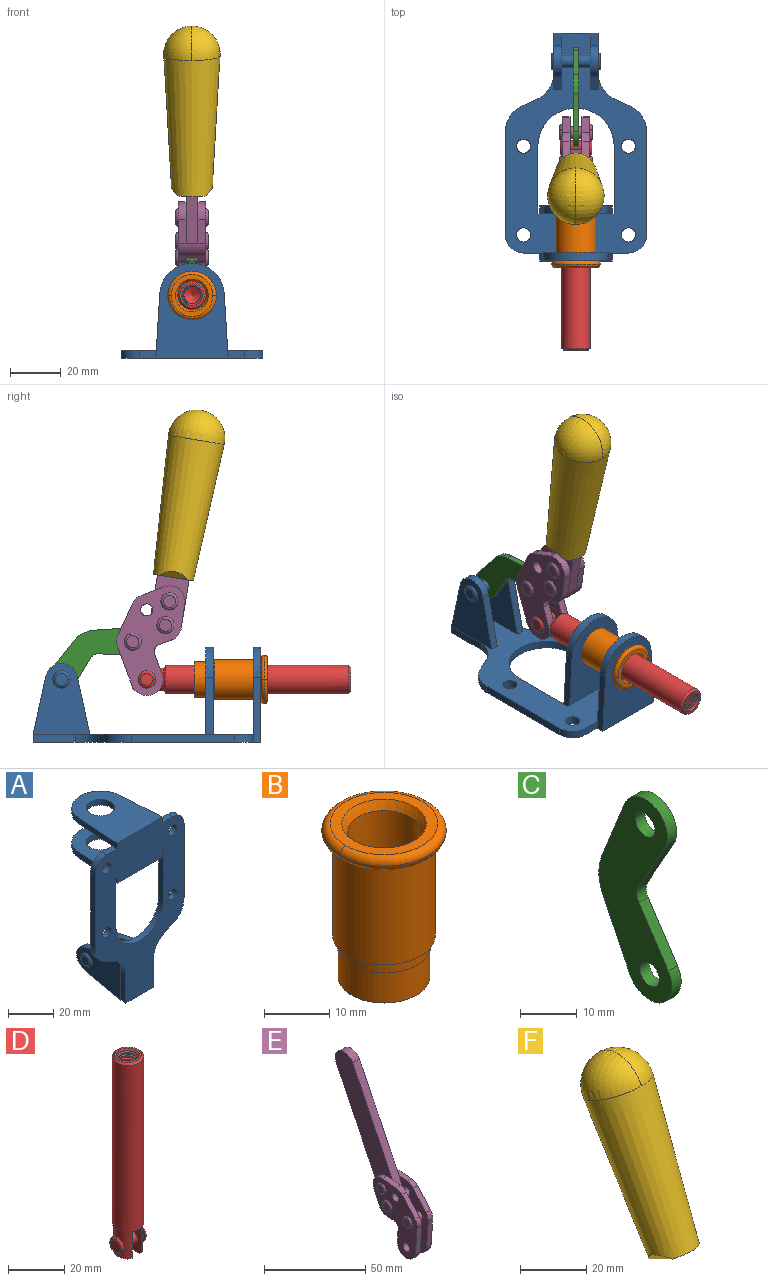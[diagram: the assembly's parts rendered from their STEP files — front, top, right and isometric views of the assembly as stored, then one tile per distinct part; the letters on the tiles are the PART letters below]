
ASSEMBLY  parts=6 mates=6
PART A: 55 faces, bbox 55.7x37.4x89.8 mm
  f0: torus R=2.41mm, axis (-1,0,0), area 15mm2, adj f11,f15,f25
  f1: torus R=2.41mm, axis (-1,0,0), area 15mm2, adj f10,f12,f22
  f2: cylinder r=2.78mm len=5.56mm, axis (0,-1,0), area 54.2mm2, adj f30,f54
  f3: cylinder r=14.99mm len=29.97mm, axis (0,-1,0), area 145.9mm2, adj f30,f49,f53,f54
  f4: cylinder r=2.78mm len=5.56mm, axis (0,-1,0), area 54.2mm2, adj f30,f54
  f5: cylinder r=2.78mm len=5.56mm, axis (0,-1,0), area 54.2mm2, adj f30,f54
  f6: cylinder r=2.78mm len=5.56mm, axis (0,-1,0), area 54.2mm2, adj f30,f54
  f7: cylinder r=6.35mm len=12.7mm, axis (0,0,1), area 123.6mm2, adj f27,f51
  f8: cylinder r=6.35mm len=12.7mm, axis (0,0,-1), area 124.7mm2, adj f21,f35
  f9: cylinder r=2.41mm len=11.18mm, axis (-1,0,0), area 169.4mm2, adj f16,f19
  f10: plane 4.83x4.83mm, normal (1,0,0), area 18.3mm2, adj f1,f12
  f11: plane 4.83x4.83mm, normal (-1,0,0), area 18.3mm2, adj f0,f15
  f12: torus R=2.41mm, axis (-1,0,0), area 15mm2, adj f1,f10,f22
  f13: cylinder r=6.35mm len=12.41mm, axis (1,0,0), area 53.4mm2, adj f18,f19,f22,f23
  f14: cylinder r=6.35mm len=12.41mm, axis (-1,0,0), area 53.4mm2, adj f16,f17,f24,f25
  f15: torus R=2.41mm, axis (-1,0,0), area 15mm2, adj f0,f11,f25
  f16: plane 27.86x22.35mm, normal (1,0,0), area 425.4mm2, adj f9,f14,f17,f24,f30
  f17: plane 22.86x4.97mm, normal (0,0.21,0.98), area 72.5mm2, adj f14,f16,f25,f30
  f18: plane 22.86x4.97mm, normal (0,0.21,0.98), area 72.5mm2, adj f13,f19,f22,f30
  f19: plane 27.86x22.35mm, normal (-1,0,0), area 425.4mm2, adj f9,f13,f18,f23,f30
  f20: cylinder r=12.7mm len=25.35mm, axis (0,0,-1), area 119.8mm2, adj f21,f34,f35,f36
  f21: plane 34.21x28.07mm, normal (0,0,-1), area 702.4mm2, adj f8,f20,f30,f34,f36
  f22: plane 27.96x22.45mm, normal (1,0,0), area 407.2mm2, adj f1,f12,f13,f18,f23,f30,f42,f43
  f23: plane 22.86x4.97mm, normal (0,0.21,-0.98), area 72.5mm2, adj f13,f19,f22,f44
  f24: plane 22.86x4.97mm, normal (0,0.21,-0.98), area 72.5mm2, adj f14,f16,f25,f44
  f25: plane 27.86x22.35mm, normal (-1,0,0), area 407.1mm2, adj f0,f14,f15,f17,f24,f30,f45,f46
  f26: plane 3.1x0.95mm, normal (0,0,-1), area 2.7mm2, adj f30,f49,f50,f54
  f27: plane 34.21x28.07mm, normal (0,0,1), area 702.4mm2, adj f7,f28,f30,f50,f52
  f28: cylinder r=12.7mm len=25.35mm, axis (0,0,1), area 118.8mm2, adj f27,f50,f51,f52
  f29: plane 3.1x0.95mm, normal (0,0,-1), area 2.7mm2, adj f30,f52,f53,f54
  f30: plane 86.54x55.63mm, normal (0,1,0), area 2362.9mm2, adj f2,f3,f4,f5,f6,f16,f17,f18
  f31: plane 40.56x3.1mm, normal (-1,0,0), area 125.7mm2, adj f30,f32,f48,f54
  f32: cylinder r=7.11mm len=7.11mm, axis (0,-1,0), area 34.6mm2, adj f30,f31,f33,f54
  f33: plane 6.67x3.1mm, normal (0,0,1), area 20.4mm2, adj f30,f32,f34,f54
  f34: plane 25.39x3.13mm, normal (-1,0.06,0), area 79.5mm2, adj f20,f21,f33,f35,f54
  f35: plane 37.31x28.45mm, normal (0,0,1), area 789.9mm2, adj f8,f20,f34,f36,f54
  f36: plane 25.39x3.13mm, normal (1,0.06,0), area 79.5mm2, adj f20,f21,f35,f37,f54
  f37: plane 6.67x3.1mm, normal (0,0,1), area 20.4mm2, adj f30,f36,f38,f54
  f38: cylinder r=7.11mm len=7.11mm, axis (0,-1,0), area 34.6mm2, adj f30,f37,f39,f54
  f39: plane 40.56x3.1mm, normal (1,0,0), area 125.7mm2, adj f30,f38,f40,f54
  f40: cylinder r=11.18mm len=10.16mm, axis (0,-1,0), area 39.5mm2, adj f30,f39,f41,f54
  f41: plane 6.09x3.1mm, normal (0.42,0,-0.91), area 20.8mm2, adj f30,f40,f42,f54
  f42: cylinder r=11.18mm len=9.41mm, axis (0,-1,0), area 37.2mm2, adj f22,f30,f41,f43,f54
  f43: plane 16.5x3.1mm, normal (1,0,0), area 51.1mm2, adj f22,f42,f44,f54
  f44: plane 17.37x3.1mm, normal (0,0,-1), area 53.8mm2, adj f23,f24,f30,f43,f45,f54
  f45: plane 16.5x3.1mm, normal (-1,0,0), area 51.1mm2, adj f25,f44,f46,f54
  f46: cylinder r=11.18mm len=9.41mm, axis (0,-1,0), area 37.2mm2, adj f25,f30,f45,f47,f54
  f47: plane 6.09x3.1mm, normal (-0.42,0,-0.91), area 20.8mm2, adj f30,f46,f48,f54
  f48: cylinder r=11.18mm len=10.16mm, axis (0,-1,0), area 39.5mm2, adj f30,f31,f47,f54
  f49: plane 26.54x3.1mm, normal (-1,0,0), area 82.3mm2, adj f3,f26,f30,f54
  f50: plane 25.39x3.1mm, normal (1,0.06,0), area 78.8mm2, adj f26,f27,f28,f51,f54
  f51: plane 37.31x28.45mm, normal (0,0,-1), area 789.9mm2, adj f7,f28,f50,f52,f54
  f52: plane 25.39x3.1mm, normal (-1,0.06,0), area 78.8mm2, adj f27,f28,f29,f51,f54
  f53: plane 26.54x3.1mm, normal (1,0,0), area 82.3mm2, adj f3,f29,f30,f54
  f54: plane 89.66x55.63mm, normal (0,-1,0), area 2678.5mm2, adj f2,f3,f4,f5,f6,f26,f29,f31
PART B: 15 faces, bbox 20.6x20.6x28.7 mm
  f0: torus R=8.26mm, axis (0,0,1), area 56.8mm2, adj f1,f10,f12
  f1: torus R=8.26mm, axis (0,0,1), area 56.8mm2, adj f0,f6,f13
  f2: cylinder r=5.59mm len=25.91mm, axis (0,0,1), area 909.6mm2, adj f3,f4
  f3: cone r=6.86mm half-angle=45deg, axis (0,0,-1), area 70.2mm2, adj f2,f14
  f4: cone r=6.47mm half-angle=30deg, axis (0,0,1), area 66.7mm2, adj f2,f13
  f5: cylinder r=7.04mm len=14.07mm, axis (0,0,1), area 252.6mm2, adj f11,f14
  f6: torus R=8.26mm, axis (0,0,1), area 56.8mm2, adj f1,f12,f13
  f7: cylinder r=7.16mm len=14.33mm, axis (0,0,1), area 91.5mm2, adj f9,f11
  f8: cylinder r=7.86mm len=18.42mm, axis (0,0,1), area 909.6mm2, adj f9,f10
  f9: plane 15.72x15.72mm, normal (0,0,-1), area 33mm2, adj f7,f8
  f10: plane 16.51x16.51mm, normal (0,0,-1), area 19.9mm2, adj f0,f8,f12
  f11: plane 14.33x14.33mm, normal (0,0,-1), area 5.7mm2, adj f5,f7
  f12: torus R=8.26mm, axis (0,0,1), area 56.8mm2, adj f0,f6,f10
  f13: plane 16.51x16.51mm, normal (0,0,1), area 82.7mm2, adj f1,f4,f6
  f14: plane 14.07x14.07mm, normal (0,0,-1), area 7.8mm2, adj f3,f5
PART C: 12 faces, bbox 2.3x18.2x42.8 mm
  f0: cylinder r=2.4mm len=4.8mm, axis (1,0,0), area 34.9mm2, adj f4,f11
  f1: cylinder r=10.41mm len=8.47mm, axis (1,0,0), area 20.2mm2, adj f4,f9,f10,f11
  f2: cylinder r=3.05mm len=3.16mm, axis (1,0,0), area 7.7mm2, adj f4,f6,f7,f11
  f3: cylinder r=2.4mm len=4.8mm, axis (1,0,0), area 34.9mm2, adj f4,f11
  f4: plane 42.81x18.23mm, normal (-1,0,0), area 414.1mm2, adj f0,f1,f2,f3,f5,f6,f7,f8
  f5: cylinder r=5.54mm len=10.67mm, axis (1,0,0), area 41.8mm2, adj f4,f6,f10,f11
  f6: plane 11.66x6.53mm, normal (0,-0.87,-0.49), area 30.9mm2, adj f2,f4,f5,f11
  f7: plane 11.17x7.33mm, normal (0,-0.84,0.55), area 30.9mm2, adj f2,f4,f8,f11
  f8: cylinder r=5.54mm len=10.51mm, axis (1,0,0), area 41.8mm2, adj f4,f7,f9,f11
  f9: plane 13.67x6.67mm, normal (0,0.9,-0.44), area 35.1mm2, adj f1,f4,f8,f11
  f10: plane 14.1x5.7mm, normal (0,0.93,0.37), area 35.1mm2, adj f1,f4,f5,f11
  f11: plane 42.81x18.23mm, normal (1,0,0), area 414.1mm2, adj f0,f1,f2,f3,f5,f6,f7,f8
PART D: 48 faces, bbox 12.6x11.1x86.1 mm
  f0: torus R=2.41mm, axis (-1,0,0), area 15mm2, adj f30,f32,f34
  f1: torus R=2.41mm, axis (-1,0,0), area 15mm2, adj f29,f31,f33
  f2: cylinder r=5.54mm len=72.39mm, axis (0,0,1), area 2518.5mm2, adj f3,f4,f42,f43
  f3: cone r=5.54mm half-angle=45deg, axis (0,0,1), area 7.6mm2, adj f2,f5,f41
  f4: cone r=5.54mm half-angle=45deg, axis (0,0,-1), area 34.9mm2, adj f2,f39
  f5: cylinder r=5.08mm len=11.48mm, axis (0,0,1), area 108.3mm2, adj f3,f7,f8,f41
  f6: cylinder r=2.41mm len=4.83mm, axis (-1,0,0), area 71.2mm2, adj f40,f41
  f7: cylinder r=2.41mm len=4.83mm, axis (-1,0,0), area 7.6mm2, adj f5,f34
  f8: cone r=5.08mm half-angle=45deg, axis (0,0,1), area 10.6mm2, adj f5,f37,f41
  f9: cone r=3.98mm half-angle=45deg, axis (0,0,1), area 17.6mm2, adj f27,f39,f45,f46,f47
  f10: cylinder r=2.41mm len=4.83mm, axis (-1,0,0), area 7.6mm2, adj f33,f38
  f11: cylinder r=3.2mm len=6.4mm, axis (0,0,1), area 78.4mm2, adj f12,f28,f44,f45,f47
  f12: cylinder r=3.2mm len=6.4mm, axis (0,0,1), area 10.5mm2, adj f11,f13,f45,f47
  f13: cylinder r=3.2mm len=6.4mm, axis (0,0,1), area 10.5mm2, adj f12,f14,f45,f47
  f14: cylinder r=3.2mm len=6.4mm, axis (0,0,1), area 10.5mm2, adj f13,f15,f45,f47
  f15: cylinder r=3.2mm len=6.4mm, axis (0,0,1), area 10.5mm2, adj f14,f16,f45,f47
  f16: cylinder r=3.2mm len=6.4mm, axis (0,0,1), area 10.5mm2, adj f15,f17,f45,f47
  f17: cylinder r=3.2mm len=6.4mm, axis (0,0,1), area 10.5mm2, adj f16,f18,f45,f47
  f18: cylinder r=3.2mm len=6.4mm, axis (0,0,1), area 10.5mm2, adj f17,f19,f45,f47
  f19: cylinder r=3.2mm len=6.4mm, axis (0,0,1), area 10.5mm2, adj f18,f20,f45,f47
  f20: cylinder r=3.2mm len=6.4mm, axis (0,0,1), area 10.5mm2, adj f19,f21,f45,f47
  f21: cylinder r=3.2mm len=6.4mm, axis (0,0,1), area 10.5mm2, adj f20,f22,f45,f47
  f22: cylinder r=3.2mm len=6.4mm, axis (0,0,1), area 10.5mm2, adj f21,f23,f45,f47
  f23: cylinder r=3.2mm len=6.4mm, axis (0,0,1), area 10.5mm2, adj f22,f24,f45,f47
  f24: cylinder r=3.2mm len=6.4mm, axis (0,0,1), area 10.5mm2, adj f23,f25,f45,f47
  f25: cylinder r=3.2mm len=6.4mm, axis (0,0,1), area 10.5mm2, adj f24,f26,f45,f47
  f26: cylinder r=3.2mm len=6.4mm, axis (0,0,1), area 10.5mm2, adj f25,f27,f45,f47
  f27: cylinder r=3.2mm len=6.4mm, axis (0,0,1), area 7.4mm2, adj f9,f26,f45,f47
  f28: cone r=3.2mm half-angle=60deg, axis (0,0,1), area 37.2mm2, adj f11
  f29: plane 4.83x4.83mm, normal (-1,0,0), area 18.3mm2, adj f1,f31
  f30: plane 4.83x4.83mm, normal (1,0,0), area 18.3mm2, adj f0,f32
  f31: torus R=2.41mm, axis (-1,0,0), area 15mm2, adj f1,f29,f33
  f32: torus R=2.41mm, axis (-1,0,0), area 15mm2, adj f0,f30,f34
  f33: plane 6.83x6.83mm, normal (1,0,0), area 18.3mm2, adj f1,f10,f31
  f34: plane 6.83x6.83mm, normal (-1,0,0), area 18.3mm2, adj f0,f7,f32
  f35: cone r=5.08mm half-angle=45deg, axis (0,0,1), area 10.6mm2, adj f36,f38,f40
  f36: plane 7.25x1.97mm, normal (0,0,-1), area 10mm2, adj f35,f40
  f37: plane 7.25x1.97mm, normal (0,0,-1), area 10mm2, adj f8,f41
  f38: cylinder r=5.08mm len=11.48mm, axis (0,0,1), area 108.3mm2, adj f10,f35,f40,f42
  f39: plane 9.55x9.55mm, normal (0,0,1), area 22mm2, adj f4,f9
  f40: plane 12.76x10.09mm, normal (1,0,0), area 95.7mm2, adj f6,f35,f36,f38,f42,f43
  f41: plane 12.76x10.09mm, normal (-1,0,0), area 95.7mm2, adj f3,f5,f6,f8,f37,f43
  f42: cone r=5.54mm half-angle=45deg, axis (0,0,1), area 7.6mm2, adj f2,f38,f40
  f43: plane 11.07x4.7mm, normal (0,0,-1), area 50.4mm2, adj f2,f40,f41
  f44: plane 0.89x0.62mm, normal (-1,0,0), area 0.3mm2, adj f11,f45,f46,f47
  f45: bspline ~24.8x7.63mm, area 266.6mm2, adj f9,f11,f12,f13,f14,f15,f16,f17
  f46: bspline ~24.87x7.63mm, area 73.6mm2, adj f9,f44,f45,f47
  f47: bspline ~24.98x7.63mm, area 272.5mm2, adj f9,f11,f12,f13,f14,f15,f16,f17
PART E: 59 faces, bbox 12.9x60.2x99.6 mm
  f0: torus R=2.39mm, axis (-1,0,0), area 14.9mm2, adj f20,f43,f51
  f1: torus R=2.39mm, axis (-1,0,0), area 14.9mm2, adj f19,f42,f51
  f2: torus R=2.39mm, axis (-1,0,0), area 14.9mm2, adj f18,f35,f51
  f3: torus R=2.39mm, axis (-1,0,0), area 14.9mm2, adj f14,f17,f23
  f4: torus R=2.39mm, axis (-1,0,0), area 14.9mm2, adj f13,f16,f23
  f5: torus R=2.39mm, axis (-1,0,0), area 14.9mm2, adj f12,f15,f23
  f6: cylinder r=2.39mm len=4.78mm, axis (1,0,0), area 46.5mm2, adj f48,f50,f51
  f7: cylinder r=2.39mm len=4.78mm, axis (1,0,0), area 46.5mm2, adj f50,f51
  f8: cylinder r=6.35mm len=12.68mm, axis (1,0,0), area 61.8mm2, adj f38,f39,f50,f51
  f9: cylinder r=2.39mm len=4.78mm, axis (-1,0,0), area 70.5mm2, adj f46,f50
  f10: cylinder r=2.39mm len=4.78mm, axis (-1,0,0), area 46.5mm2, adj f23,f45,f46
  f11: cylinder r=2.39mm len=4.78mm, axis (-1,0,0), area 46.5mm2, adj f23,f46
  f12: plane 4.78x4.78mm, normal (1,0,0), area 17.9mm2, adj f5,f15
  f13: plane 4.78x4.78mm, normal (1,0,0), area 17.9mm2, adj f4,f16
  f14: plane 4.78x4.78mm, normal (1,0,0), area 17.9mm2, adj f3,f17
  f15: torus R=2.39mm, axis (-1,0,0), area 14.9mm2, adj f5,f12,f23
  f16: torus R=2.39mm, axis (-1,0,0), area 14.9mm2, adj f4,f13,f23
  f17: torus R=2.39mm, axis (-1,0,0), area 14.9mm2, adj f3,f14,f23
  f18: plane 4.78x4.78mm, normal (-1,0,0), area 17.9mm2, adj f2,f35
  f19: plane 4.78x4.78mm, normal (-1,0,0), area 17.9mm2, adj f1,f42
  f20: plane 4.78x4.78mm, normal (-1,0,0), area 17.9mm2, adj f0,f43
  f21: plane 2.26x0.2mm, normal (1,0,0), area 0.2mm2, adj f31,f44
  f22: plane 2.26x0.2mm, normal (-1,0,0), area 0.2mm2, adj f41,f44
  f23: plane 39.37x30.77mm, normal (1,0,0), area 565.5mm2, adj f3,f4,f5,f10,f11,f15,f16,f17
  f24: cylinder r=6.1mm len=4.15mm, axis (-1,0,0), area 14.7mm2, adj f23,f25,f32,f46
  f25: plane 10.25x9.01mm, normal (0,-0.75,0.66), area 42.3mm2, adj f23,f24,f26,f46
  f26: cylinder r=6.35mm len=4.64mm, axis (-1,0,0), area 15.6mm2, adj f23,f25,f27,f46
  f27: plane 15.84x3.1mm, normal (0,-1,-0.07), area 49.2mm2, adj f23,f26,f28,f46
  f28: cylinder r=6.35mm len=12.68mm, axis (-1,0,0), area 61.8mm2, adj f23,f27,f29,f46
  f29: plane 8.11x3.1mm, normal (0,1,0.07), area 25.2mm2, adj f23,f28,f30,f46
  f30: cylinder r=3.05mm len=3.25mm, axis (-1,0,0), area 14.8mm2, adj f23,f29,f31,f46
  f31: plane 5.99x3.1mm, normal (0,0.07,-1), area 18.6mm2, adj f21,f23,f30,f44,f46
  f32: plane 9.5x3.1mm, normal (0,-0.07,1), area 29.5mm2, adj f23,f24,f33,f46,f47
  f33: cylinder r=6.1mm len=8.63mm, axis (-1,0,0), area 39.1mm2, adj f23,f32,f34,f47
  f34: plane 8.65x3.96mm, normal (0,0.91,-0.42), area 29.5mm2, adj f23,f33,f44,f47
  f35: torus R=2.39mm, axis (-1,0,0), area 14.9mm2, adj f2,f18,f51
  f36: plane 10.25x9.01mm, normal (0,-0.75,0.66), area 42.3mm2, adj f37,f49,f50,f51
  f37: cylinder r=6.35mm len=4.64mm, axis (1,0,0), area 15.6mm2, adj f36,f38,f50,f51
  f38: plane 15.84x3.1mm, normal (0,-1,-0.07), area 49.2mm2, adj f8,f37,f50,f51
  f39: plane 8.11x3.1mm, normal (0,1,0.07), area 25.2mm2, adj f8,f40,f50,f51
  f40: cylinder r=3.05mm len=3.25mm, axis (1,0,0), area 14.8mm2, adj f39,f41,f50,f51
  f41: plane 5.99x3.1mm, normal (0,0.07,-1), area 18.6mm2, adj f22,f40,f44,f50,f51
  f42: torus R=2.39mm, axis (-1,0,0), area 14.9mm2, adj f1,f19,f51
  f43: torus R=2.39mm, axis (-1,0,0), area 14.9mm2, adj f0,f20,f51
  f44: cylinder r=6.35mm len=12.12mm, axis (-1,0,0), area 128.9mm2, adj f21,f22,f23,f31,f34,f41,f46,f47
  f45: plane 2.65x1.35mm, normal (1,0,0), area 1mm2, adj f10,f55
  f46: plane 39.08x20.42mm, normal (-1,0,0), area 412.5mm2, adj f9,f10,f11,f24,f25,f26,f27,f28
  f47: plane 77.62x39.82mm, normal (1,0,0), area 850mm2, adj f32,f33,f34,f44,f53,f54,f55
  f48: plane 2.65x1.35mm, normal (-1,0,0), area 1mm2, adj f6,f55
  f49: cylinder r=6.1mm len=4.15mm, axis (1,0,0), area 14.7mm2, adj f36,f50,f51,f56
  f50: plane 39.08x20.42mm, normal (1,0,0), area 412.5mm2, adj f6,f7,f8,f9,f36,f37,f38,f39
  f51: plane 39.37x30.77mm, normal (-1,0,0), area 565.5mm2, adj f0,f1,f2,f6,f7,f8,f35,f36
  f52: plane 8.65x3.96mm, normal (0,0.91,-0.42), area 29.5mm2, adj f44,f51,f57,f58
  f53: plane 68.49x33.4mm, normal (0,0.9,-0.44), area 358.1mm2, adj f44,f47,f54,f58
  f54: cylinder r=6.35mm len=12.06mm, axis (1,0,0), area 93.7mm2, adj f47,f53,f55,f58
  f55: plane 68.49x33.4mm, normal (0,-0.9,0.44), area 358.1mm2, adj f44,f45,f46,f47,f48,f50,f54,f58
  f56: plane 9.5x3.1mm, normal (0,-0.07,1), area 29.5mm2, adj f49,f50,f51,f57,f58
  f57: cylinder r=6.1mm len=8.63mm, axis (1,0,0), area 39.1mm2, adj f51,f52,f56,f58
  f58: plane 77.62x39.82mm, normal (-1,0,0), area 850mm2, adj f44,f52,f53,f54,f55,f56,f57
PART F: 11 faces, bbox 22.3x42.6x64.5 mm
  f0: sphere r=11.13mm, area 411.4mm2, adj f1,f8
  f1: cone r=11.11mm half-angle=3.3deg, axis (0,0.44,0.9), area 3251.8mm2, adj f0,f7,f8,f9,f10
  f2: cylinder r=6.16mm len=11.7mm, axis (1,0,0), area 89.5mm2, adj f3,f4,f5,f6
  f3: plane 60.23x36.75mm, normal (-1,0,0), area 763.6mm2, adj f2,f4,f6,f10
  f4: plane 51.37x25.05mm, normal (0,0.9,-0.44), area 264.2mm2, adj f2,f3,f5,f10
  f5: plane 60.23x36.75mm, normal (1,0,0), area 763.6mm2, adj f2,f4,f6,f10
  f6: plane 51.37x25.05mm, normal (0,-0.9,0.44), area 264.2mm2, adj f2,f3,f5,f10
  f7: plane 9.95x5.95mm, normal (0.71,-0.31,-0.64), area 25.8mm2, adj f1,f10
  f8: sphere r=11.13mm, area 411.4mm2, adj f0,f1
  f9: plane 9.95x5.95mm, normal (-0.71,-0.31,-0.64), area 25.8mm2, adj f1,f10
  f10: plane 14.27x11.38mm, normal (0,-0.44,-0.9), area 106.7mm2, adj f1,f3,f4,f5,f6,f7,f9
PLACE A rot(axis=(1,0,0),90deg) t=(0,9.43,0)mm fixed
PLACE B rot(axis=(1,0,0),90deg) t=(0,9.43,0)mm
PLACE C rot(axis=(1,0,0),64.1deg) t=(0,16.63,10.58)mm
PLACE D rot(axis=(1,0,0),90deg) t=(0,23.37,0)mm
PLACE E rot(axis=(0,-0.14,-0.99),180deg) t=(0,40.63,48.38)mm
PLACE F rot(axis=(0,0.14,0.99),180deg) t=(-0.04,40.63,48.38)mm
MATE fastened F.f2 <-> E.f54  axis (1,0,0) through (-2.35,-11.89,121.1)mm
MATE revolute D.f6 <-> E.f7  axis (-1,0,0) through (0,7.9,24.61)mm
MATE revolute C.f5 <-> E.f4  axis (1,0,0) through (0,13.47,39.48)mm
MATE fastened B.f2 <-> A.f7  axis (0,1,0) through (0,-36.96,24.61)mm
MATE revolute C.f3 <-> A.f0  axis (1,0,0) through (0,41.52,24.61)mm
MATE slider D.f2 <-> A.f7  axis (0,-1,0) through (0,-35.41,24.61)mm
